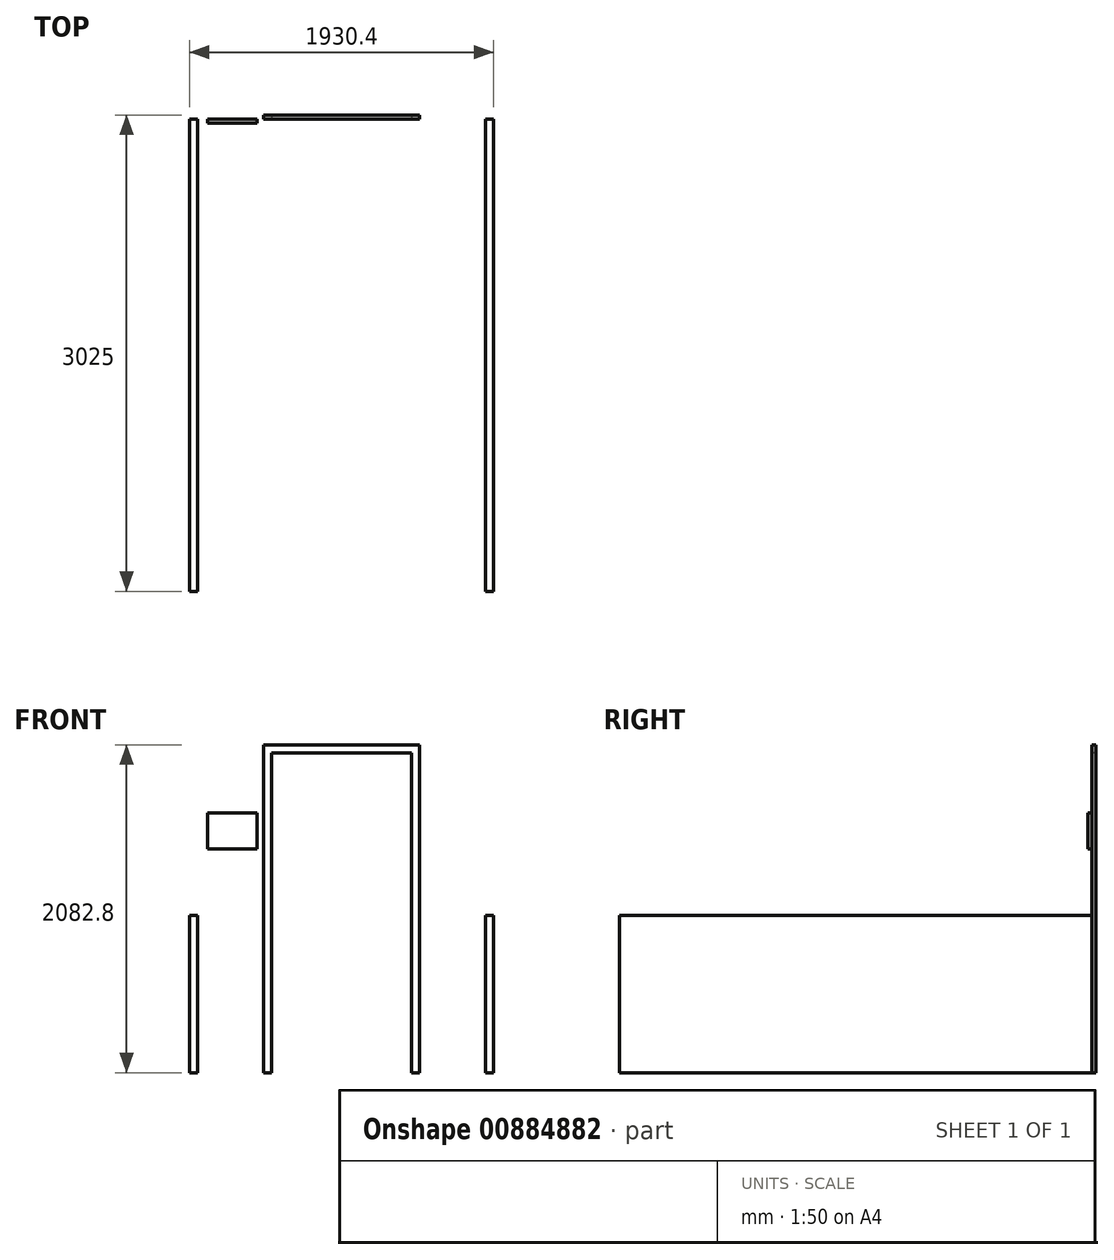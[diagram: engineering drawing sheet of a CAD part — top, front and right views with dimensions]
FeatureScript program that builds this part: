
annotation { "Feature Type Name" : "Feature", "Feature Type Description" : "" }
export const myFeature = defineFeature(function(context is Context, id is Id, definition is map)
    precondition{}
    {
        {
            var Q0;
            Q0=qCreatedBy(makeId("Top.planeOp"),FACE);
            var sketch = newSketch(context, id + "F0", { "sketchPlane" : qUnion([Q0])});
            skLineSegment(sketch, "E0.bottom", {"start": v(-965.2, 0) * mm, "end": v(-914.4, 0) * mm});
            skLineSegment(sketch, "E0.top", {"start": v(-965.2, -3000) * mm, "end": v(-914.4, -3000) * mm});
            skLineSegment(sketch, "E0.left", {"start": v(-965.2, 0) * mm, "end": v(-965.2, -3000) * mm});
            skLineSegment(sketch, "E0.right", {"start": v(-914.4, 0) * mm, "end": v(-914.4, -3000) * mm});
            skSolve(sketch);
        }
        {
            var Q0;
            Q0=makeQuery(id+"F0.imprint","IMPRINT",FACE,{"disambiguationData":[TD([[makeQuery(id+"F0.imprint","IMPRINT",EDGE,{"derivedFrom":sQuery(id+"F0.wireOp",EDGE,"E0.bottom")}),-1.0]])]});
            extrude(context, id + "F1", {"entities" : qUnion([Q0]), "depth" : 1000 * mm, "offsetDistance" : 25 * mm});
        }
        {
            var Q0;
            Q0=makeQuery(id+"F1.opExtrude","SWEPT_BODY",BODY,{"disambiguationData":[OSD([sQuery(id+"F0.wireOp",EDGE,"E0.bottom"),sQuery(id+"F0.wireOp",EDGE,"E0.top"),sQuery(id+"F0.wireOp",EDGE,"E0.left"),sQuery(id+"F0.wireOp",EDGE,"E0.right")])]});
            var Q1;
            Q1=qCreatedBy(makeId("Right.planeOp"),FACE);
            mirror(context, id + "F2", {"entities" : qUnion([Q0]), "mirrorPlane" : qUnion([Q1])});
        }
        {
            var Q0;
            Q0=qCreatedBy(makeId("Front.planeOp"),FACE);
            var sketch = newSketch(context, id + "F3", { "sketchPlane" : qUnion([Q0])});
            skLineSegment(sketch, "E1.bottom", {"start": v(-444.5, 2032) * mm, "end": v(444.5, 2032) * mm});
            skLineSegment(sketch, "E1.top", {"start": v(-444.5, 0) * mm, "end": v(444.5, 0) * mm});
            skLineSegment(sketch, "E1.left", {"start": v(-444.5, 2032) * mm, "end": v(-444.5, 0) * mm});
            skLineSegment(sketch, "E1.right", {"start": v(444.5, 2032) * mm, "end": v(444.5, 0) * mm});
            skLineSegment(sketch, "E2.bottom", {"start": v(-495.3, 0) * mm, "end": v(495.3, 0) * mm});
            skLineSegment(sketch, "E2.top", {"start": v(-495.3, 2082.8) * mm, "end": v(495.3, 2082.8) * mm});
            skLineSegment(sketch, "E2.left", {"start": v(-495.3, 0) * mm, "end": v(-495.3, 2082.8) * mm});
            skLineSegment(sketch, "E2.right", {"start": v(495.3, 0) * mm, "end": v(495.3, 2082.8) * mm});
            skSolve(sketch);
        }
        {
            var Q0;
            Q0=makeQuery(id+"F3.imprint","IMPRINT",FACE,{"disambiguationData":[TD([[makeQuery(id+"F3.imprint","IMPRINT",EDGE,{"derivedFrom":sQuery(id+"F3.wireOp",EDGE,"E1.bottom")}),1.0]])]});
            extrude(context, id + "F4", {"entities" : qUnion([Q0]), "oppositeDirection" : true, "depth" : 25 * mm, "offsetDistance" : 25 * mm});
        }
        {
            var Q0;
            Q0=qCreatedBy(makeId("Front.planeOp"),FACE);
            var sketch = newSketch(context, id + "F5", { "sketchPlane" : qUnion([Q0])});
            skLineSegment(sketch, "E3.bottom", {"start": v(-851.92, 1648.58) * mm, "end": v(-536.32, 1648.58) * mm});
            skLineSegment(sketch, "E3.top", {"start": v(-851.92, 1422.4) * mm, "end": v(-536.32, 1422.4) * mm});
            skLineSegment(sketch, "E3.left", {"start": v(-851.92, 1648.58) * mm, "end": v(-851.92, 1422.4) * mm});
            skLineSegment(sketch, "E3.right", {"start": v(-536.32, 1648.58) * mm, "end": v(-536.32, 1422.4) * mm});
            skSolve(sketch);
        }
        {
            var Q0;
            Q0=makeQuery(id+"F5.imprint","IMPRINT",FACE,{"disambiguationData":[TD([[makeQuery(id+"F5.imprint","IMPRINT",EDGE,{"derivedFrom":sQuery(id+"F5.wireOp",EDGE,"E3.bottom")}),-1.0]])]});
            extrude(context, id + "F6", {"entities" : qUnion([Q0]), "depth" : 25 * mm, "offsetDistance" : 25 * mm});
        }
    });
